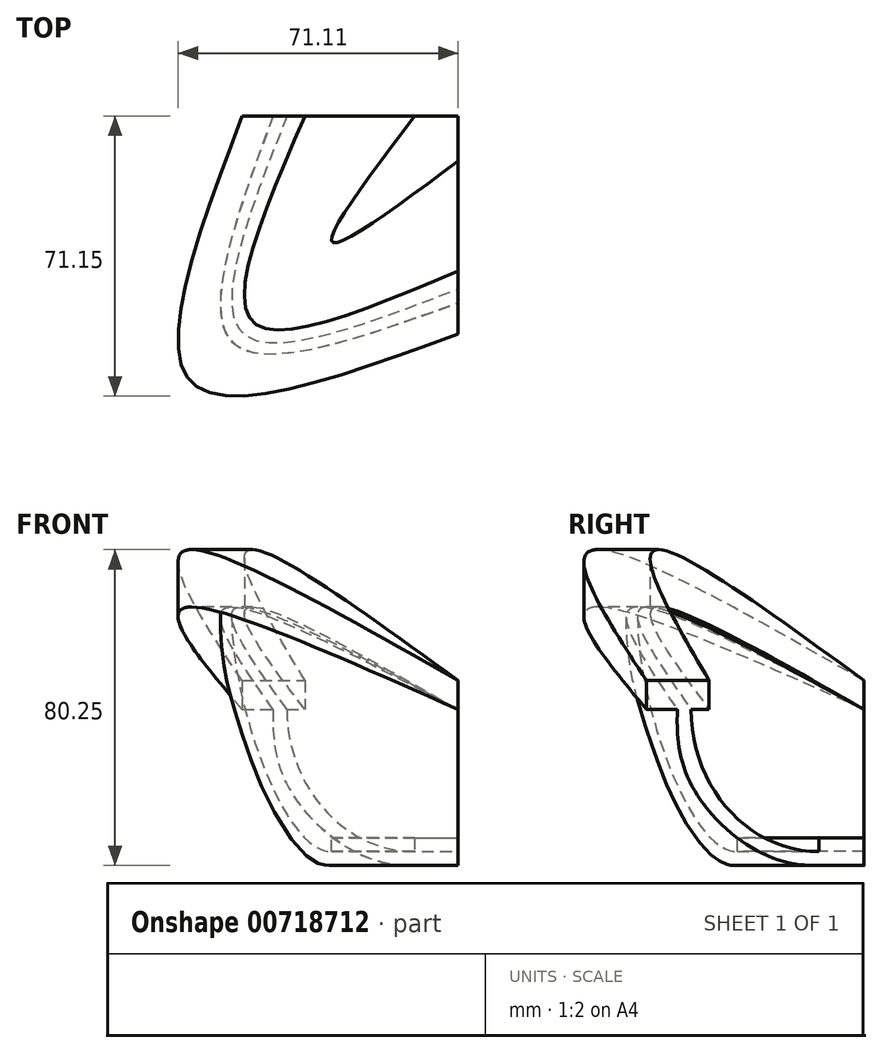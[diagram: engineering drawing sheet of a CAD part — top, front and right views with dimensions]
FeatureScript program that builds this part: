
annotation { "Feature Type Name" : "Feature", "Feature Type Description" : "" }
export const myFeature = defineFeature(function(context is Context, id is Id, definition is map)
    precondition{}
    {
        {
            var Q0;
            Q0=qCreatedBy(makeId("Front.planeOp"),FACE);
            var sketch = newSketch(context, id + "F0", { "sketchPlane" : qUnion([Q0])});
            skLineSegment(sketch, "E0.bottom", {"start": v(-54.87, 46.95) * mm, "end": v(-38.92, 46.95) * mm});
            skLineSegment(sketch, "E0.top", {"start": v(-54.87, 39.6) * mm, "end": v(-38.92, 39.6) * mm});
            skLineSegment(sketch, "E0.left", {"start": v(-54.87, 46.95) * mm, "end": v(-54.87, 39.6) * mm});
            skLineSegment(sketch, "E0.right", {"start": v(-38.92, 46.95) * mm, "end": v(-38.92, 39.6) * mm});
            skLineSegment(sketch, "E1.bottom", {"start": v(-11.01, 7) * mm, "end": v(0, 7) * mm});
            skLineSegment(sketch, "E1.top", {"start": v(-11.01, 0) * mm, "end": v(0, 0) * mm});
            skLineSegment(sketch, "E1.left", {"start": v(-11.01, 7) * mm, "end": v(-11.01, 0) * mm});
            skLineSegment(sketch, "E1.right", {"start": v(0, 7) * mm, "end": v(0, 0) * mm});
            skFitSpline(sketch, "E2", {"points": [v(-43.47, 39.6) * mm, v(-11.01, 3.5) * mm], "startDerivative": vector(0, -59.35) * mm, "endDerivative": vector(53.62, 0) * mm});
            skFitSpline(sketch, "E3.0", {"points": [v(-46.97, 39.6) * mm, v(-46.97, 34.23) * mm, v(-44.99, 23.93) * mm, v(-38.48, 13.27) * mm, v(-31.38, 6.72) * mm, v(-25.24, 2.97) * mm, v(-18.4, 0.57) * mm, v(-13.51, 0) * mm, v(-11.01, 0) * mm]});
            skSolve(sketch);
        }
        {
            var Q0;
            Q0=qCreatedBy(makeId("Right.planeOp"),FACE);
            var sketch = newSketch(context, id + "F1", { "sketchPlane" : qUnion([Q0])});
            skLineSegment(sketch, "E4.bottom", {"start": v(-55.32, 46.95) * mm, "end": v(-39.37, 46.95) * mm});
            skLineSegment(sketch, "E4.top", {"start": v(-55.32, 39.6) * mm, "end": v(-39.37, 39.6) * mm});
            skLineSegment(sketch, "E4.left", {"start": v(-55.32, 46.95) * mm, "end": v(-55.32, 39.6) * mm});
            skLineSegment(sketch, "E4.right", {"start": v(-39.37, 46.95) * mm, "end": v(-39.37, 39.6) * mm});
            skLineSegment(sketch, "E5.bottom", {"start": v(-11.46, 7) * mm, "end": v(0, 7) * mm});
            skLineSegment(sketch, "E5.top", {"start": v(-11.46, 0) * mm, "end": v(0, 0) * mm});
            skLineSegment(sketch, "E5.left", {"start": v(-11.46, 7) * mm, "end": v(-11.46, 0) * mm});
            skLineSegment(sketch, "E5.right", {"start": v(0, 7) * mm, "end": v(0, 0) * mm});
            skFitSpline(sketch, "E6", {"points": [v(-43.92, 39.6) * mm, v(-11.46, 3.5) * mm], "startDerivative": vector(0, -59.35) * mm, "endDerivative": vector(53.62, 0) * mm});
            skFitSpline(sketch, "E7.0", {"points": [v(-47.42, 39.6) * mm, v(-47.42, 34.23) * mm, v(-45.44, 23.93) * mm, v(-38.93, 13.27) * mm, v(-31.83, 6.72) * mm, v(-25.69, 2.97) * mm, v(-18.86, 0.57) * mm, v(-13.96, 0) * mm, v(-11.46, 0) * mm]});
            skSolve(sketch);
        }
        {
            var Q0;
            Q0=sQuery(id+"F1.wireOp",EDGE,"E5.right");
            cPlane(context, id + "F2", {"entities" : qUnion([Q0]), "cplaneType" : CPlaneType.LINE_ANGLE, "offset" : 25 * mm, "angle" : 225 * degree, "width" : 150 * mm, "height" : 150 * mm});
        }
        {
            var Q0;
            Q0=qCreatedBy(id+"F2.planeOp",FACE);
            var sketch = newSketch(context, id + "F3", { "sketchPlane" : qUnion([Q0])});
            skLineSegment(sketch, "E8.bottom", {"start": v(-95.73, 80.23) * mm, "end": v(-73.83, 80.23) * mm});
            skLineSegment(sketch, "E8.top", {"start": v(-95.73, 65.66) * mm, "end": v(-73.83, 65.66) * mm});
            skLineSegment(sketch, "E8.left", {"start": v(-95.73, 80.23) * mm, "end": v(-95.73, 65.66) * mm});
            skLineSegment(sketch, "E8.right", {"start": v(-73.83, 80.23) * mm, "end": v(-73.83, 65.66) * mm});
            skLineSegment(sketch, "E9.bottom", {"start": v(-45.24, 7) * mm, "end": v(0, 7) * mm});
            skLineSegment(sketch, "E9.top", {"start": v(-45.24, 0) * mm, "end": v(0, 0) * mm});
            skLineSegment(sketch, "E9.left", {"start": v(-45.24, 7) * mm, "end": v(-45.24, 0) * mm});
            skLineSegment(sketch, "E9.right", {"start": v(0, 7) * mm, "end": v(0, 0) * mm});
            skFitSpline(sketch, "E10", {"points": [v(-77.7, 65.66) * mm, v(-45.24, 3.5) * mm], "startDerivative": vector(0, -59.35) * mm, "endDerivative": vector(53.62, 0) * mm});
            skFitSpline(sketch, "E11.0", {"points": [v(-81.2, 65.66) * mm, v(-81.2, 64.32) * mm, v(-81.08, 61.49) * mm, v(-80.38, 55.33) * mm, v(-78.73, 46.87) * mm, v(-75.62, 36.15) * mm, v(-71.51, 25.58) * mm, v(-67.33, 17.49) * mm, v(-63.55, 11.79) * mm, v(-60.48, 7.99) * mm, v(-57.17, 4.75) * mm, v(-53.55, 2.18) * mm, v(-49.58, 0.44) * mm, v(-46.7, 0) * mm, v(-45.24, 0) * mm]});
            skSolve(sketch);
        }
        {
            var Q0;
            Q0 = qSketchRegion(id + "F0", true);
            var Q1;
            Q1 = qSketchRegion(id + "F3", true);
            var Q2;
            Q2 = qSketchRegion(id + "F1", true);
            var Q3;
            Q3=sQuery(id+"F1.wireOp",EDGE,"E4.bottom");
            var Q4;
            Q4=sQuery(id+"F3.wireOp",EDGE,"E8.bottom");
            var Q5;
            Q5=sQuery(id+"F0.wireOp",EDGE,"E0.bottom");
            loft(context, id + "F4", {"sheetProfilesArray" : [{ "sheetProfileEntities" : qUnion([Q0]) }, { "sheetProfileEntities" : qUnion([Q1]) }, { "sheetProfileEntities" : qUnion([Q2]) }], "guidesArray" : [{ "guideEntities" : qUnion([Q3]), "guideDerivativeType" : LoftGuideDerivativeType.DEFAULT, "guideDerivativeMagnitude" : 1 }, { "guideEntities" : qUnion([Q4]), "guideDerivativeType" : LoftGuideDerivativeType.DEFAULT, "guideDerivativeMagnitude" : 1 }, { "guideEntities" : qUnion([Q5]), "guideDerivativeType" : LoftGuideDerivativeType.DEFAULT, "guideDerivativeMagnitude" : 1 }]});
        }
    });
